# Revit family: RFAHP105
name_source: partatom
category: Generic Models
revit_build: Autodesk Revit MEP 2013 (Build: 20130531_2115(x64)
units: mm (PartAtom-declared; Revit-internal decimal feet)

## types (1)
- Hydroboil Plus HP105
    Base Unit Finish = Stainless Steel.
    Button Interface = Liquid crystal display panel, button controls
    Cable Length and size (If Fitted) = Not fitted
    Capacity = 5.0 Litres
    Control Thermostat Range = 68°C  -- 100°C
    Enclosure Rating = IP23
    External Material = Stainless Steel case
    Gross Weight = 16.5kg (When full)
    Heat Up Time = 16 minutes at 15°C  and 17 minutes 10°C
    Insulation Material = High temperature thermal insulation (High density EP)
    Mains Pressure Limiting Valve = If pressure is likely to exceed 0.7 MPa (7 bar), a pressure limiting valve must be fitted
be installed in the cold water supply line. Zip recommends a valve rated at 3.5 bar
(0.35 MPa) for this application (Zip part No. AQ3).
    Mains Water Connection = 1/2 inch / 12.7mm compression fitting
    Mains Water Pressure _ Maximum = 0.7 MPa (7 bar).
    Mains Water Pressure _ Minimum = 0.07 MPa (0.7 bar)
    Manufacturer = Zip Industries(UK) Ltd
    Max. Stored Water Temperature = 98°C
    Model = HP105
    Net Weight = 9.5kg
    Overall Height = 465mm
    Overall Length/Depth = 198mm
    Overall Width = 318mm
    Power Rating = 2.4kW
    Power Supply (Voltage) = 230v(50~60Hz)
    Product Range = Wall Mounted
    Programmable Function Parameters = The Hydroboil Plus has 2 modes of operation: 1).Normal operation mode  2). Configuration mode									
The Hydroboil Plus has 2 modes of operation: 1).Normal operation mode  2). Configuration mode
    Programmable Safety Features = Integral safety lock
    Quarterly Maintenance (or SFG20 Codes) = In some hard water areas where mineral scale accumulation in the boilingchamber of the Zip Econoboil may become a problem, consideration should be given to the maintenance required.
chamber of the Zip Econoboil may become a problem, consideration should be
given to the maintenance required. 
necessary.
    Shape = Rectangle
    Shipping Weight = 9.5kg
    Single Instance Draw off Volume = 3.0 litres
    Supply Phase = Single, A standard 13 amp double pole fused spur
    Tank Construction Material = Stainless Steel
    Tap Clearance = 200mm
    Tap Finish = Red Lever in Display Panel
    Type = On The Wall Water Boiler
    Type Comments = Boiling Water Heater (Potable)
    URL = www.zipindustries.co.uk
    Unit Access Clearance Bottom = 200mm
    Unit Access Clearance Left = 65mm
    Unit Access Clearance Top = 150mm
    Unit Access Clearance right = 20mm
    Volume Dispensed per hour = 16.7litres
    WRAS Approved = Yes

## geometry (parser evidence)
native form markers: Sweep x3
no freeform markers — native parametric forms only
